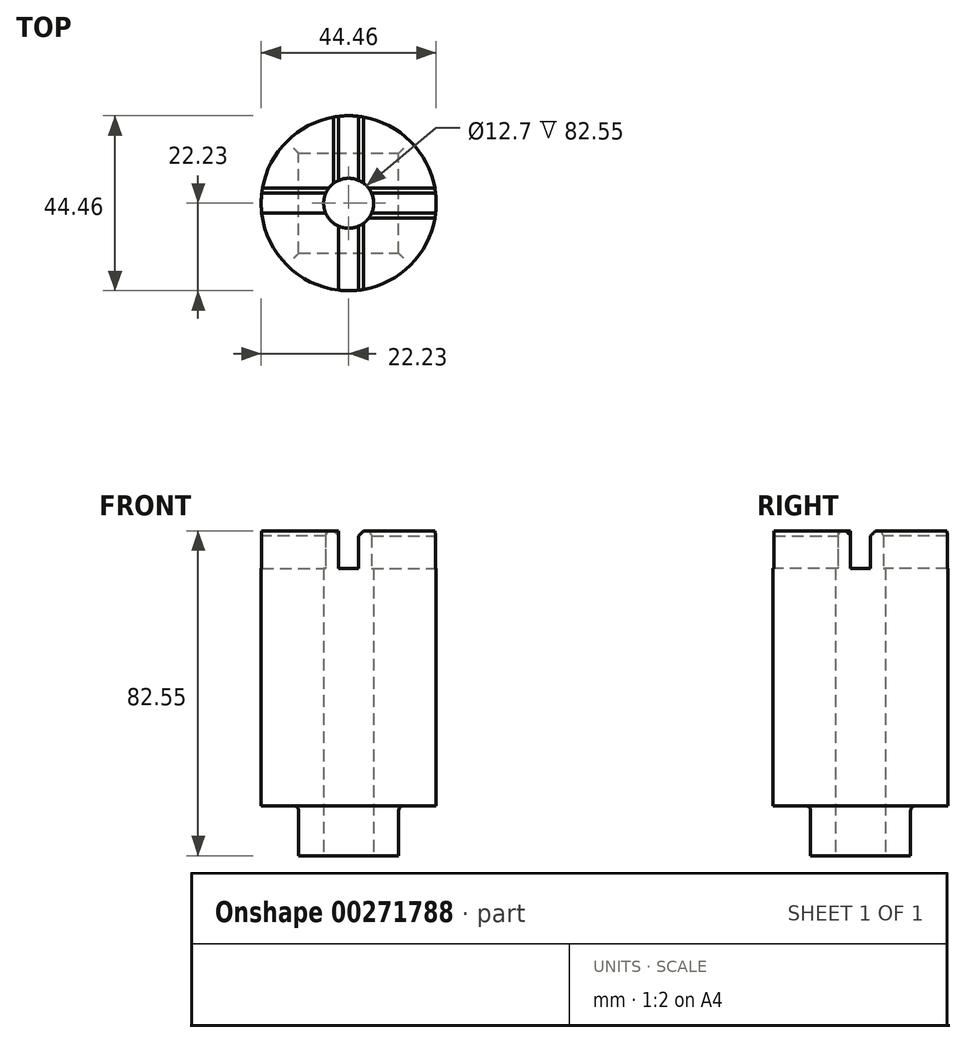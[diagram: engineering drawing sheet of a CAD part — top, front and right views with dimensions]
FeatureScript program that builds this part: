
annotation { "Feature Type Name" : "Feature", "Feature Type Description" : "" }
export const myFeature = defineFeature(function(context is Context, id is Id, definition is map)
    precondition{}
    {
        {
            var Q0;
            Q0=qCreatedBy(makeId("Top.planeOp"),FACE);
            var sketch = newSketch(context, id + "F0", { "sketchPlane" : qUnion([Q0])});
            skCircle(sketch, "E0", {"center": v(0, 0) * mm, "radius": 22.23 * mm});
            skSolve(sketch);
        }
        {
            var Q0;
            Q0=makeQuery(id+"F0.imprint","IMPRINT",FACE,{"disambiguationData":[TD([[makeQuery(id+"F0.imprint","IMPRINT",EDGE,{"derivedFrom":sQuery(id+"F0.wireOp",EDGE,"E0")}),1.0]])]});
            extrude(context, id + "F1", {"entities" : qUnion([Q0]), "depth" : 82.55 * mm});
        }
        {
            var Q0;
            Q0=makeQuery(id+"F1.opExtrude","CAP_FACE",FACE,{"disambiguationData":[OSD([sQuery(id+"F0.wireOp",EDGE,"E0")])],"isStart":false});
            var sketch = newSketch(context, id + "F2", { "sketchPlane" : qUnion([Q0])});
            skLineSegment(sketch, "E1", {"start": v(-2.54, 22.08) * mm, "end": v(-2.54, 2.54) * mm});
            skLineSegment(sketch, "E2", {"start": v(2.54, 22.08) * mm, "end": v(2.54, 2.54) * mm});
            skLineSegment(sketch, "E3", {"start": v(-22.08, 2.54) * mm, "end": v(-2.54, 2.54) * mm});
            skLineSegment(sketch, "E4", {"start": v(-22.08, -2.54) * mm, "end": v(-2.54, -2.54) * mm});
            skLineSegment(sketch, "E5.trimOffspring", {"start": v(-2.54, -2.54) * mm, "end": v(-2.54, -22.08) * mm});
            skLineSegment(sketch, "E6.trimOffspring", {"start": v(2.54, 2.54) * mm, "end": v(22.08, 2.54) * mm});
            skLineSegment(sketch, "E7.trimOffspring", {"start": v(2.54, -2.54) * mm, "end": v(2.54, -22.08) * mm});
            skLineSegment(sketch, "E8.trimOffspring", {"start": v(2.54, -2.54) * mm, "end": v(22.08, -2.54) * mm});
            skArc(sketch, "E9", {"start": v(-22.08, 2.54) * mm, "mid": v(-22.23, 0) * mm, "end": v(-22.08, -2.54) * mm});
            skArc(sketch, "E10.trimOffspring", {"start": v(2.54, 22.08) * mm, "mid": v(0, 22.23) * mm, "end": v(-2.54, 22.08) * mm});
            skArc(sketch, "E11.trimOffspring", {"start": v(22.08, -2.54) * mm, "mid": v(22.22, 0) * mm, "end": v(22.08, 2.54) * mm});
            skArc(sketch, "E12.trimOffspring", {"start": v(-2.54, -22.08) * mm, "mid": v(0, -22.23) * mm, "end": v(2.54, -22.08) * mm});
            skSolve(sketch);
        }
        {
            var Q0;
            Q0=makeQuery(id+"F2.imprint","IMPRINT",FACE,{"disambiguationData":[TD([[makeQuery(id+"F2.imprint","IMPRINT",EDGE,{"derivedFrom":sQuery(id+"F2.wireOp",EDGE,"E1")}),1.0]])]});
            extrude(context, id + "F3", {"entities" : qUnion([Q0]), "operationType" : NewBodyOperationType.REMOVE, "oppositeDirection" : true, "depth" : 9.52 * mm});
        }
        {
            var Q0;
            Q0=makeQuery(id+"F3.boolean.opBoolean","COPY",EDGE,{"derivedFrom":makeQuery(id+"F3.opExtrude","CAP_EDGE",EDGE,{"disambiguationData":[OSD([sQuery(id+"F2.wireOp",EDGE,"E3")])],"isStart":true})});
            var Q1;
            Q1=makeQuery(id+"F3.boolean.opBoolean","COPY",EDGE,{"derivedFrom":makeQuery(id+"F3.opExtrude","CAP_EDGE",EDGE,{"disambiguationData":[OSD([sQuery(id+"F2.wireOp",EDGE,"E1")])],"isStart":true})});
            var Q2;
            Q2=makeQuery(id+"F3.boolean.opBoolean","COPY",EDGE,{"derivedFrom":makeQuery(id+"F3.opExtrude","CAP_EDGE",EDGE,{"disambiguationData":[OSD([sQuery(id+"F2.wireOp",EDGE,"E2")])],"isStart":true})});
            var Q3;
            Q3=makeQuery(id+"F3.boolean.opBoolean","COPY",EDGE,{"derivedFrom":makeQuery(id+"F3.opExtrude","CAP_EDGE",EDGE,{"disambiguationData":[OSD([sQuery(id+"F2.wireOp",EDGE,"E6.trimOffspring")])],"isStart":true})});
            var Q4;
            Q4=makeQuery(id+"F3.boolean.opBoolean","COPY",EDGE,{"derivedFrom":makeQuery(id+"F3.opExtrude","CAP_EDGE",EDGE,{"disambiguationData":[OSD([sQuery(id+"F2.wireOp",EDGE,"E8.trimOffspring")])],"isStart":true})});
            var Q5;
            Q5=makeQuery(id+"F3.boolean.opBoolean","COPY",EDGE,{"derivedFrom":makeQuery(id+"F3.opExtrude","CAP_EDGE",EDGE,{"disambiguationData":[OSD([sQuery(id+"F2.wireOp",EDGE,"E7.trimOffspring")])],"isStart":true})});
            var Q6;
            Q6=makeQuery(id+"F3.boolean.opBoolean","COPY",EDGE,{"derivedFrom":makeQuery(id+"F3.opExtrude","CAP_EDGE",EDGE,{"disambiguationData":[OSD([sQuery(id+"F2.wireOp",EDGE,"E5.trimOffspring")])],"isStart":true})});
            var Q7;
            Q7=makeQuery(id+"F3.boolean.opBoolean","COPY",EDGE,{"derivedFrom":makeQuery(id+"F3.opExtrude","CAP_EDGE",EDGE,{"disambiguationData":[OSD([sQuery(id+"F2.wireOp",EDGE,"E4")])],"isStart":true})});
            chamfer(context, id + "F4", {"entities" : qUnion([Q0, Q1, Q2, Q3, Q4, Q5, Q6, Q7]), "width" : 1.27 * mm, "tangentPropagation" : true});
        }
        {
            var Q0;
            Q0=makeQuery(id+"F1.opExtrude","CAP_FACE",FACE,{"disambiguationData":[OSD([sQuery(id+"F0.wireOp",EDGE,"E0")])],"isStart":true});
            var sketch = newSketch(context, id + "F5", { "sketchPlane" : qUnion([Q0])});
            skLineSegment(sketch, "E13.bottom", {"start": v(-12.7, 12.7) * mm, "end": v(12.7, 12.7) * mm});
            skLineSegment(sketch, "E13.top", {"start": v(-12.7, -12.7) * mm, "end": v(12.7, -12.7) * mm});
            skLineSegment(sketch, "E13.left", {"start": v(-12.7, 12.7) * mm, "end": v(-12.7, -12.7) * mm});
            skLineSegment(sketch, "E13.right", {"start": v(12.7, 12.7) * mm, "end": v(12.7, -12.7) * mm});
            skSolve(sketch);
        }
        {
            var Q0;
            Q0=makeQuery(id+"F5.imprint","IMPRINT",FACE,{"disambiguationData":[TD([[makeQuery(id+"F5.imprint","IMPRINT",EDGE,{"derivedFrom":sQuery(id+"F5.wireOp",EDGE,"E13.bottom")}),1.0]])]});
            extrude(context, id + "F6", {"entities" : qUnion([Q0]), "operationType" : NewBodyOperationType.REMOVE, "oppositeDirection" : true, "depth" : 12.7 * mm});
        }
        {
            var Q0;
            Q0=makeQuery(id+"F6.boolean.opBoolean","COPY",EDGE,{"derivedFrom":makeQuery(id+"F6.opExtrude","CAP_EDGE",EDGE,{"disambiguationData":[OSD([sQuery(id+"F5.wireOp",EDGE,"E13.top")])],"isStart":false})});
            var Q1;
            Q1=makeQuery(id+"F6.boolean.opBoolean","COPY",EDGE,{"derivedFrom":makeQuery(id+"F6.opExtrude","CAP_EDGE",EDGE,{"disambiguationData":[OSD([sQuery(id+"F5.wireOp",EDGE,"E13.right")])],"isStart":false})});
            var Q2;
            Q2=makeQuery(id+"F6.boolean.opBoolean","COPY",EDGE,{"derivedFrom":makeQuery(id+"F6.opExtrude","CAP_EDGE",EDGE,{"disambiguationData":[OSD([sQuery(id+"F5.wireOp",EDGE,"E13.left")])],"isStart":false})});
            var Q3;
            Q3=makeQuery(id+"F6.boolean.opBoolean","COPY",EDGE,{"derivedFrom":makeQuery(id+"F6.opExtrude","CAP_EDGE",EDGE,{"disambiguationData":[OSD([sQuery(id+"F5.wireOp",EDGE,"E13.bottom")])],"isStart":false})});
            fillet(context, id + "F7", {"entities" : qUnion([Q0, Q1, Q2, Q3]), "radius" : 1.27 * mm, "tangentPropagation" : true, "allowEdgeOverflow" : false});
        }
        {
            var Q0;
            Q0=makeQuery(id+"F1.opExtrude","CAP_FACE",FACE,{"disambiguationData":[OSD([sQuery(id+"F0.wireOp",EDGE,"E0")])],"isStart":true});
            var sketch = newSketch(context, id + "F8", { "sketchPlane" : qUnion([Q0])});
            skCircle(sketch, "E14", {"center": v(0, 0) * mm, "radius": 6.35 * mm});
            skSolve(sketch);
        }
        {
            var Q0;
            Q0=makeQuery(id+"F8.imprint","IMPRINT",FACE,{"disambiguationData":[TD([[makeQuery(id+"F8.imprint","IMPRINT",EDGE,{"derivedFrom":sQuery(id+"F8.wireOp",EDGE,"E14")}),1.0]])]});
            extrude(context, id + "F9", {"entities" : qUnion([Q0]), "operationType" : NewBodyOperationType.REMOVE, "endBound" : BoundingType.THROUGH_ALL, "oppositeDirection" : true, "depth" : 25.4 * mm});
        }
    });
